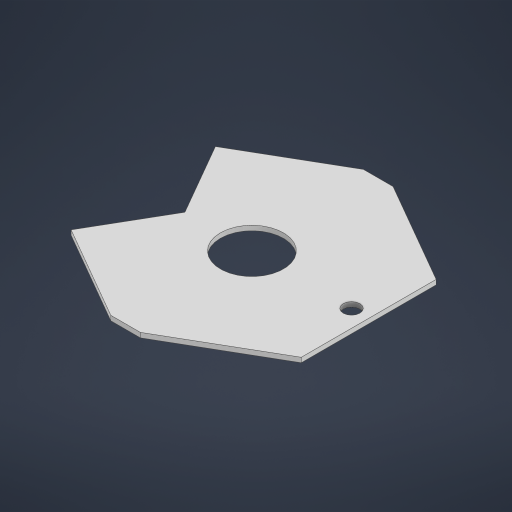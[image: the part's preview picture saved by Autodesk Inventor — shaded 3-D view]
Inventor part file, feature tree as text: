
AUTODESK INVENTOR PART (.ipt)
format: ipt  version: 2023 (Build 270158000, 158)  size: 186,368 bytes
history: native  units: in
note: dims shown in document units (in); Inventor stores cm internally (conversion verified against a paired STEP export)
features: extrude x2, sketch x1
ambient origin geometry x8: Origin, YZ Plane, XZ Plane, XY Plane, X Axis, Y Axis, Z Axis, Center Point
bodies: Solid1 (feature_tree)
feature tree (3):
  sketch  "Sketch1"  dims[d0=0.5217in d1=1.939in d2=0.0394in d3=0.0in d4=120.0deg d5=120.0deg d6=0.4134in d7=0.9695in d8=0.0709in d9=0.0709in d10=0.1378in d11=0.8268in d12=0.0in d13=0.0in]
  extrude  "Extrusion1"  Depth=1.939in
  extrude  "Extrusion2"  Depth=0.0394in TaperAngle=0.0deg
